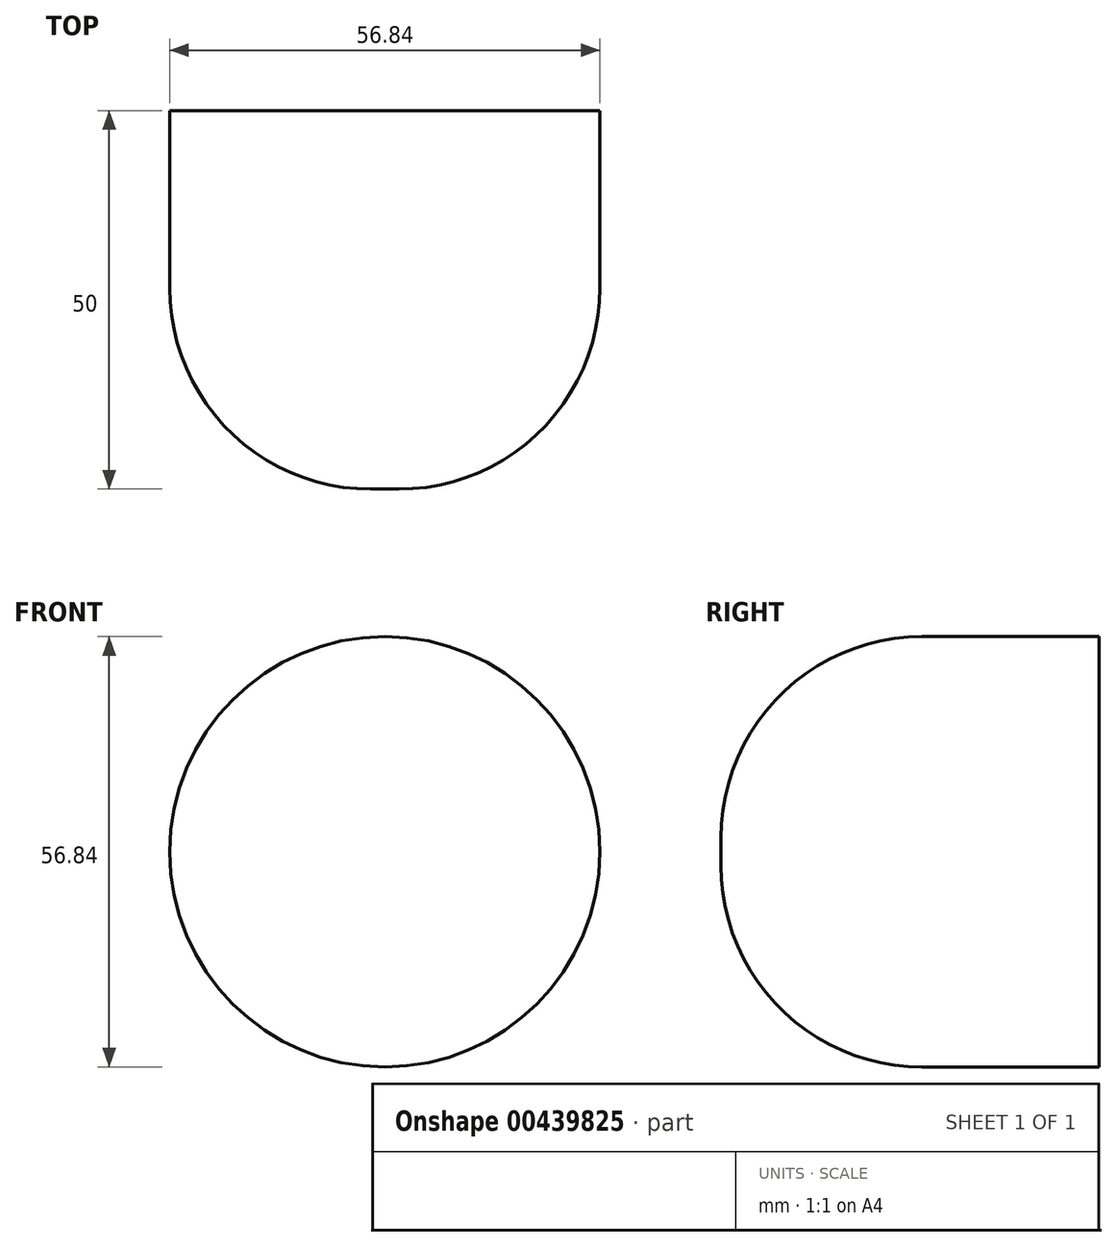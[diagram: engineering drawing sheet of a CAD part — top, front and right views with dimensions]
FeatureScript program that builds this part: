
annotation { "Feature Type Name" : "Feature", "Feature Type Description" : "" }
export const myFeature = defineFeature(function(context is Context, id is Id, definition is map)
    precondition{}
    {
        {
            var Q0;
            Q0=qCreatedBy(makeId("Front.planeOp"),FACE);
            var sketch = newSketch(context, id + "F0", { "sketchPlane" : qUnion([Q0])});
            skCircle(sketch, "E0", {"center": v(0, 0) * mm, "radius": 28.42 * mm});
            skSolve(sketch);
        }
        {
            var Q0;
            Q0 = qSketchRegion(id + "F0", true);
            extrude(context, id + "F1", {"entities" : qUnion([Q0]), "depth" : 50 * mm, "offsetDistance" : 25 * mm});
        }
        {
            var Q0;
            Q0=makeQuery(id+"F1.opExtrude","CAP_EDGE",EDGE,{"disambiguationData":[OSD([sQuery(id+"F0.wireOp",EDGE,"E0")])],"isStart":false});
            fillet(context, id + "F2", {"entities" : qUnion([Q0]), "radius" : 26.56 * mm, "tangentPropagation" : true, "allowEdgeOverflow" : false});
        }
    });
